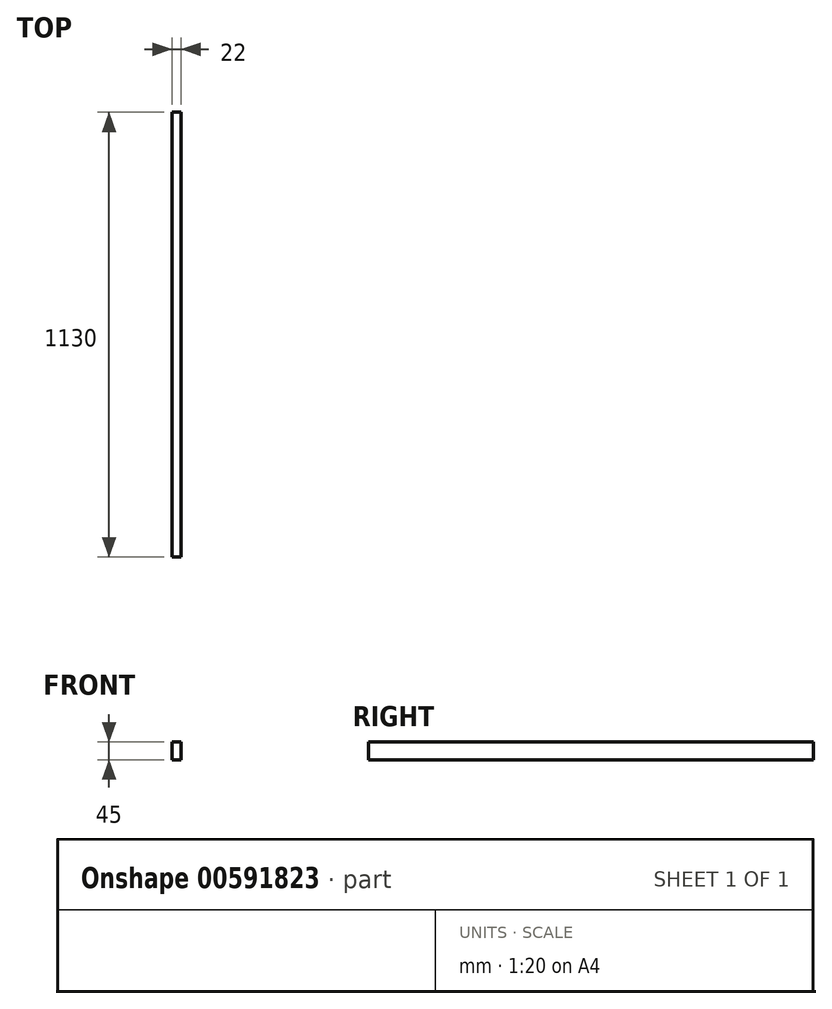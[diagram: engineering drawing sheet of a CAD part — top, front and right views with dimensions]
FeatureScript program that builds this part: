
annotation { "Feature Type Name" : "Feature", "Feature Type Description" : "" }
export const myFeature = defineFeature(function(context is Context, id is Id, definition is map)
    precondition{}
    {
        {
            var Q0;
            Q0=qCreatedBy(makeId("Front.planeOp"),FACE);
            var sketch = newSketch(context, id + "F0", { "sketchPlane" : qUnion([Q0])});
            skLineSegment(sketch, "E0.bottom", {"start": v(0, 0) * mm, "end": v(22, 0) * mm});
            skLineSegment(sketch, "E0.top", {"start": v(0, 45) * mm, "end": v(22, 45) * mm});
            skLineSegment(sketch, "E0.left", {"start": v(0, 0) * mm, "end": v(0, 45) * mm});
            skLineSegment(sketch, "E0.right", {"start": v(22, 0) * mm, "end": v(22, 45) * mm});
            skSolve(sketch);
        }
        {
            var Q0;
            Q0=qSketchRegion(id+"F0",true);
            extrude(context, id + "F1", {"entities" : qUnion([Q0]), "depth" : 1130 * mm, "offsetDistance" : 25 * mm});
        }
    });
